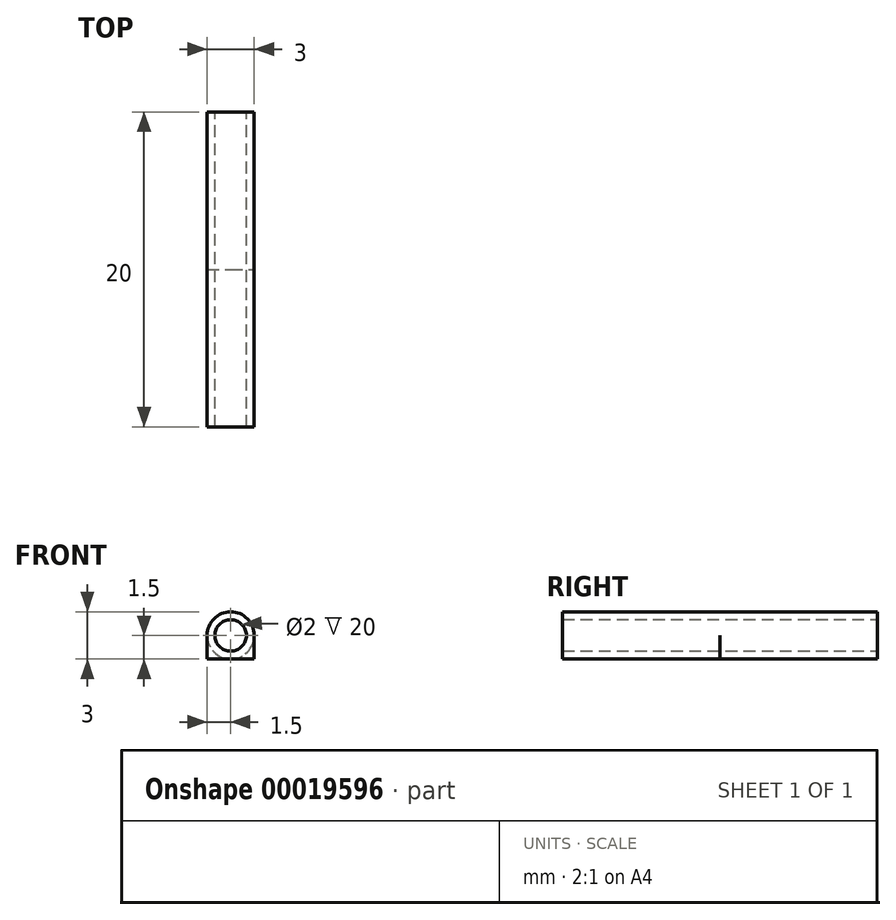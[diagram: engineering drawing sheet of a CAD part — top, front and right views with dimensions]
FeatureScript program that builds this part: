
annotation { "Feature Type Name" : "Feature", "Feature Type Description" : "" }
export const myFeature = defineFeature(function(context is Context, id is Id, definition is map)
    precondition{}
    {
        {
            var Q0;
            Q0=qCreatedBy(makeId("Front.planeOp"),FACE);
            var sketch = newSketch(context, id + "F0", { "sketchPlane" : qUnion([Q0])});
            skCircle(sketch, "E0", {"center": v(0, 0) * mm, "radius": 1 * mm});
            skCircle(sketch, "E1", {"center": v(0, 0) * mm, "radius": 1.5 * mm});
            skSolve(sketch);
        }
        {
            var Q0;
            Q0 = qSketchRegion(id + "F0", true);
            extrude(context, id + "F1", {"entities" : qUnion([Q0]), "depth" : 20 * mm});
        }
        {
            var Q0;
            Q0=makeQuery(id+"F1.opExtrude","CAP_FACE",FACE,{"disambiguationData":[OSD([sQuery(id+"F0.wireOp",EDGE,"E0"),sQuery(id+"F0.wireOp",EDGE,"E1")])],"isStart":false});
            var sketch = newSketch(context, id + "F2", { "sketchPlane" : qUnion([Q0])});
            skLineSegment(sketch, "E2", {"start": v(-1.5, -1.5) * mm, "end": v(1.5, -1.5) * mm});
            skLineSegment(sketch, "E3", {"start": v(-1.5, 0) * mm, "end": v(-1.5, -1.5) * mm});
            skLineSegment(sketch, "E4", {"start": v(1.5, 0) * mm, "end": v(1.5, -1.5) * mm});
            skArc(sketch, "E5", {"start": v(-1.5, 0) * mm, "mid": v(0, -1.5) * mm, "end": v(1.5, 0) * mm});
            skSolve(sketch);
        }
        {
            var Q0;
            Q0 = qSketchRegion(id + "F2", true);
            extrude(context, id + "F3", {"entities" : qUnion([Q0]), "operationType" : NewBodyOperationType.ADD, "oppositeDirection" : true, "depth" : 10 * mm});
        }
    });
